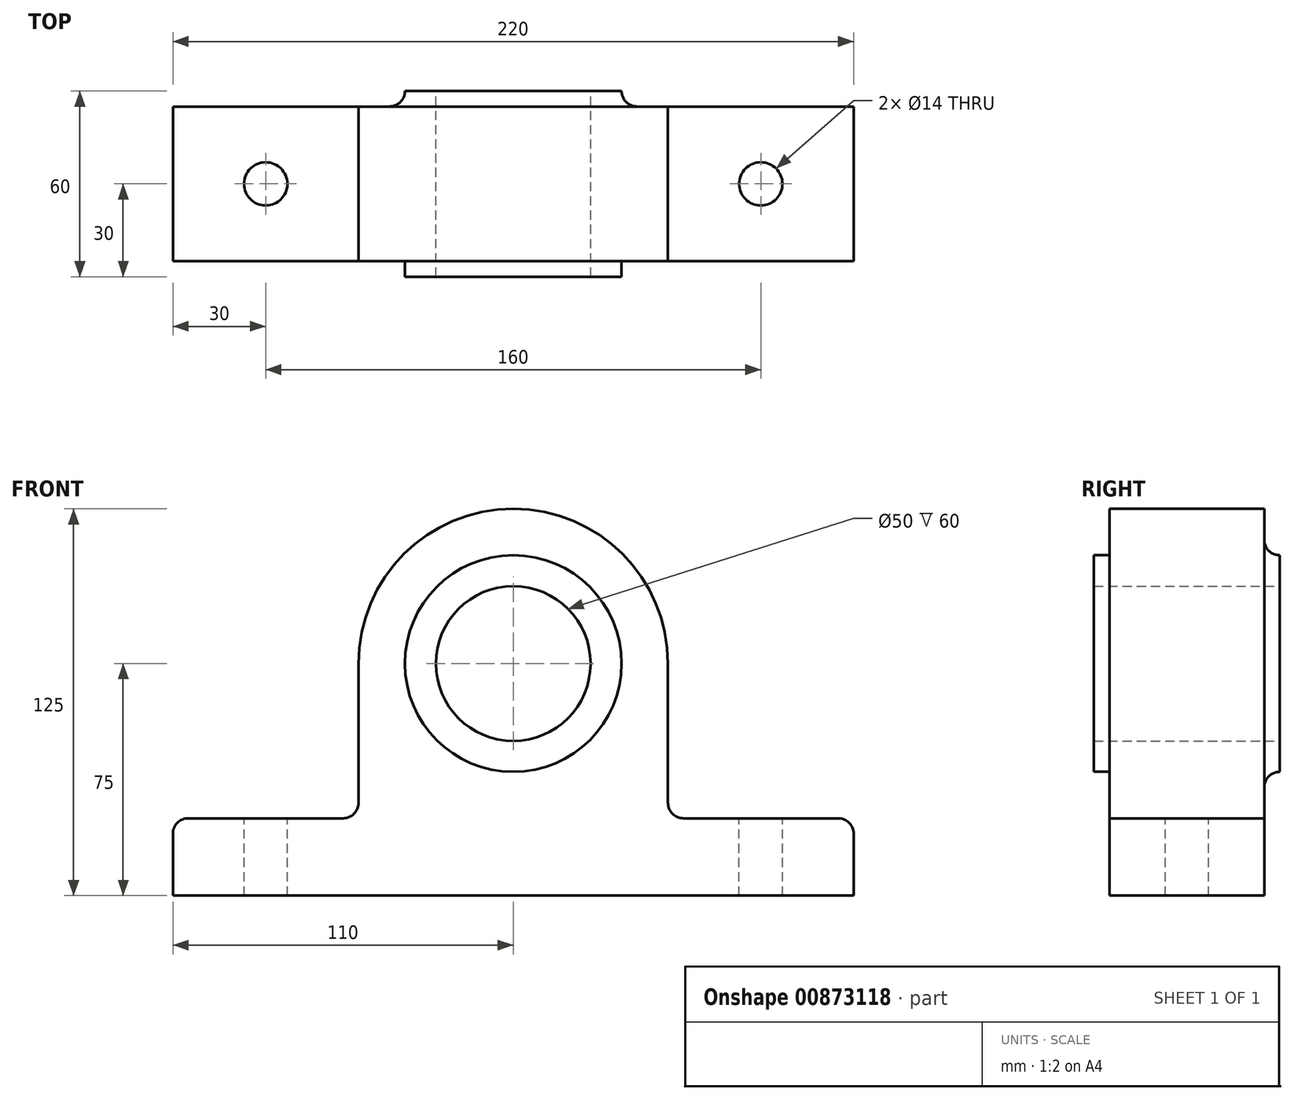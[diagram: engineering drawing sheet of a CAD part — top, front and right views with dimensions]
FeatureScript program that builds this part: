
annotation { "Feature Type Name" : "Feature", "Feature Type Description" : "" }
export const myFeature = defineFeature(function(context is Context, id is Id, definition is map)
    precondition{}
    {
        {
            var Q0;
            Q0=qCreatedBy(makeId("Front.planeOp"),FACE);
            var sketch = newSketch(context, id + "F0", { "sketchPlane" : qUnion([Q0])});
            skCircle(sketch, "E0", {"center": v(0, 0) * mm, "radius": 25 * mm});
            skCircle(sketch, "E1", {"center": v(0, 0) * mm, "radius": 32.5 * mm});
            skCircle(sketch, "E2", {"center": v(0, 0) * mm, "radius": 50 * mm});
            skPoint(sketch, "E3.start.orphan", {"position": v(-50, 0) * mm});
            skLineSegment(sketch, "E4", {"start": v(-50, 0) * mm, "end": v(-50, -50) * mm});
            skLineSegment(sketch, "E5", {"start": v(50, 0) * mm, "end": v(50, -50) * mm});
            skLineSegment(sketch, "E6", {"start": v(50, -50) * mm, "end": v(110, -50) * mm});
            skLineSegment(sketch, "E7", {"start": v(-50, -50) * mm, "end": v(-110, -50) * mm});
            skLineSegment(sketch, "E8", {"start": v(-110, -50) * mm, "end": v(-110, -75) * mm});
            skLineSegment(sketch, "E9", {"start": v(-110, -75) * mm, "end": v(110, -75) * mm});
            skLineSegment(sketch, "E10", {"start": v(110, -75) * mm, "end": v(110, -50) * mm});
            skSolve(sketch);
        }
        {
            var Q0;
            Q0 = qSketchRegion(id + "F0", true);
            var Q1;
            Q1=makeQuery(id+"F0.imprint","IMPRINT",FACE,{"disambiguationData":[TD([[makeQuery(id+"F0.imprint","IMPRINT",EDGE,{"derivedFrom":sQuery(id+"F0.wireOp",EDGE,"E0")}),-1.0]])]});
            extrude(context, id + "F1", {"entities" : qUnion([Q0, Q1]), "depth" : 50 * mm, "offsetDistance" : 25 * mm});
        }
        {
            var Q0;
            Q0=makeQuery(id+"F1.opExtrude","SWEPT_FACE",FACE,{"disambiguationData":[OSD([sQuery(id+"F0.wireOp",EDGE,"E7")])]});
            var sketch = newSketch(context, id + "F2", { "sketchPlane" : qUnion([Q0])});
            skCircle(sketch, "E11", {"center": v(-80, -25) * mm, "radius": 8.89 * mm});
            skPoint(sketch, "E11.centerSnap0", {"position": v(-80, -50) * mm});
            skPoint(sketch, "E11.centerSnap1", {"position": v(-110, -25) * mm});
            skSolve(sketch);
        }
        {
            var Q0;
            Q0=makeQuery(id+"F1.opExtrude","SWEPT_FACE",FACE,{"disambiguationData":[OSD([sQuery(id+"F0.wireOp",EDGE,"E6")])]});
            var sketch = newSketch(context, id + "F3", { "sketchPlane" : qUnion([Q0])});
            skCircle(sketch, "E12", {"center": v(80, -25) * mm, "radius": 8 * mm});
            skPoint(sketch, "E12.centerSnap0", {"position": v(110, -25) * mm});
            skPoint(sketch, "E12.centerSnap1", {"position": v(80, -50) * mm});
            skSolve(sketch);
        }
        {
            var Q0;
            Q0=sQuery(id+"F2.wireOp",VERTEX,"E11.center");
            var Q1;
            Q1=sQuery(id+"F3.wireOp",VERTEX,"E12.center");
            var Q2;
            Q2=makeQuery(id+"F1.opExtrude","SWEPT_BODY",BODY,{"disambiguationData":[OSD([sQuery(id+"F0.wireOp",EDGE,"E0"),sQuery(id+"F0.wireOp",EDGE,"E2"),sQuery(id+"F0.wireOp",EDGE,"E4"),sQuery(id+"F0.wireOp",EDGE,"E5"),sQuery(id+"F0.wireOp",EDGE,"E6"),sQuery(id+"F0.wireOp",EDGE,"E7"),sQuery(id+"F0.wireOp",EDGE,"E8"),sQuery(id+"F0.wireOp",EDGE,"E9"),sQuery(id+"F0.wireOp",EDGE,"E10")])]});
            hole(context, id + "F4", {"style" : HoleStyle.SIMPLE, "endStyle" : HoleEndStyle.THROUGH, "standardTappedOrClearance" : lookupTablePath({ "standard" : "ISO", "engagement" : "75%", "pitch" : "2 mm", "size" : "M16", "type" : "Tapped" }), "standardBlindInLast" : lookupTablePath({ "standard" : "ISO", "engagement" : "75%", "pitch" : "2 mm", "size" : "M16", "type" : "Tapped" }), "holeDiameter" : 14 * mm, "majorDiameter" : 16 * mm, "showTappedDepth" : true, "isTappedThrough" : true, "tappedDepth" : 14 * mm, "tapClearance" : 3, "locations" : qUnion([Q0, Q1]), "scope" : qUnion([Q2])});
        }
        {
            var Q0;
            Q0=makeQuery(id+"F1.opExtrude","SWEPT_EDGE",EDGE,{"disambiguationData":[OSD([sQuery(id+"F0.wireOp",EDGE,"E5"),sQuery(id+"F0.wireOp",EDGE,"E6")])]});
            var Q1;
            Q1=makeQuery(id+"F1.opExtrude","SWEPT_EDGE",EDGE,{"disambiguationData":[OSD([sQuery(id+"F0.wireOp",EDGE,"E4"),sQuery(id+"F0.wireOp",EDGE,"E7")])]});
            var Q2;
            Q2=makeQuery(id+"F1.opExtrude","SWEPT_EDGE",EDGE,{"disambiguationData":[OSD([sQuery(id+"F0.wireOp",EDGE,"E6"),sQuery(id+"F0.wireOp",EDGE,"E10")])]});
            var Q3;
            Q3=makeQuery(id+"F1.opExtrude","SWEPT_EDGE",EDGE,{"disambiguationData":[OSD([sQuery(id+"F0.wireOp",EDGE,"E7"),sQuery(id+"F0.wireOp",EDGE,"E8")])]});
            fillet(context, id + "F5", {"entities" : qUnion([Q0, Q1, Q2, Q3]), "radius" : 5 * mm, "tangentPropagation" : true, "allowEdgeOverflow" : false});
        }
        {
            var Q0;
            Q0=makeQuery(id+"F1.opExtrude","CAP_FACE",FACE,{"disambiguationData":[OSD([sQuery(id+"F0.wireOp",EDGE,"E0"),sQuery(id+"F0.wireOp",EDGE,"E2"),sQuery(id+"F0.wireOp",EDGE,"E4"),sQuery(id+"F0.wireOp",EDGE,"E5"),sQuery(id+"F0.wireOp",EDGE,"E6"),sQuery(id+"F0.wireOp",EDGE,"E7"),sQuery(id+"F0.wireOp",EDGE,"E8"),sQuery(id+"F0.wireOp",EDGE,"E9"),sQuery(id+"F0.wireOp",EDGE,"E10")])],"isStart":true});
            var sketch = newSketch(context, id + "F6", { "sketchPlane" : qUnion([Q0])});
            skCircle(sketch, "E13", {"center": v(0, 0) * mm, "radius": 35 * mm});
            skSolve(sketch);
        }
        {
            var Q0;
            Q0=makeQuery(id+"F6.imprint","IMPRINT",FACE,{"disambiguationData":[TD([[makeQuery(id+"F6.imprint","IMPRINT",EDGE,{"derivedFrom":sQuery(id+"F6.wireOp",EDGE,"E13")}),1.0]])]});
            extrude(context, id + "F7", {"entities" : qUnion([Q0]), "operationType" : NewBodyOperationType.ADD, "oppositeDirection" : true, "depth" : 50 * mm, "offsetDistance" : 25 * mm});
        }
        {
            var Q0;
            Q0=makeQuery(id+"F1.opExtrude","CAP_FACE",FACE,{"disambiguationData":[OSD([sQuery(id+"F0.wireOp",EDGE,"E0"),sQuery(id+"F0.wireOp",EDGE,"E2"),sQuery(id+"F0.wireOp",EDGE,"E4"),sQuery(id+"F0.wireOp",EDGE,"E5"),sQuery(id+"F0.wireOp",EDGE,"E6"),sQuery(id+"F0.wireOp",EDGE,"E7"),sQuery(id+"F0.wireOp",EDGE,"E8"),sQuery(id+"F0.wireOp",EDGE,"E9"),sQuery(id+"F0.wireOp",EDGE,"E10")])],"isStart":false});
            var sketch = newSketch(context, id + "F8", { "sketchPlane" : qUnion([Q0])});
            skCircle(sketch, "E14", {"center": v(0, 0) * mm, "radius": 35 * mm});
            skSolve(sketch);
        }
        {
            var Q0;
            Q0=makeQuery(id+"F8.imprint","IMPRINT",FACE,{"disambiguationData":[TD([[makeQuery(id+"F8.imprint","IMPRINT",EDGE,{"derivedFrom":sQuery(id+"F8.wireOp",EDGE,"E14")}),1.0]])]});
            extrude(context, id + "F9", {"entities" : qUnion([Q0]), "operationType" : NewBodyOperationType.ADD, "depth" : 5 * mm, "offsetDistance" : 25 * mm});
        }
        {
            var Q0;
            Q0=makeQuery(id+"F9.opExtrude","CAP_FACE",FACE,{"disambiguationData":[OSD([sQuery(id+"F0.wireOp",EDGE,"E0"),sQuery(id+"F8.wireOp",EDGE,"E14")])],"isStart":false});
            extrude(context, id + "F10", {"entities" : qUnion([Q0]), "operationType" : NewBodyOperationType.ADD, "oppositeDirection" : true, "depth" : 60 * mm, "offsetDistance" : 25 * mm});
        }
        {
            var Q0;
            Q0=makeQuery(id+"F9.opExtrude","CAP_EDGE",EDGE,{"disambiguationData":[OSD([sQuery(id+"F8.wireOp",EDGE,"E14")])],"isStart":true});
            var Q1;
            Q1=makeQuery(id+"F10.boolean.opBoolean","INTERSECT",EDGE,{"derivedFrom":[makeQuery(id+"F1.opExtrude","CAP_FACE",FACE,{"disambiguationData":[OSD([sQuery(id+"F0.wireOp",EDGE,"E0"),sQuery(id+"F0.wireOp",EDGE,"E2"),sQuery(id+"F0.wireOp",EDGE,"E4"),sQuery(id+"F0.wireOp",EDGE,"E5"),sQuery(id+"F0.wireOp",EDGE,"E6"),sQuery(id+"F0.wireOp",EDGE,"E7"),sQuery(id+"F0.wireOp",EDGE,"E8"),sQuery(id+"F0.wireOp",EDGE,"E9"),sQuery(id+"F0.wireOp",EDGE,"E10")])],"isStart":true}),makeQuery(id+"F10.opExtrude","SWEPT_FACE",FACE,{"disambiguationData":[OSD([sQuery(id+"F8.wireOp",EDGE,"E14")])]})]});
            fillet(context, id + "F11", {"entities" : qUnion([Q0, Q1]), "radius" : 5 * mm, "tangentPropagation" : true, "allowEdgeOverflow" : false});
        }
    });
